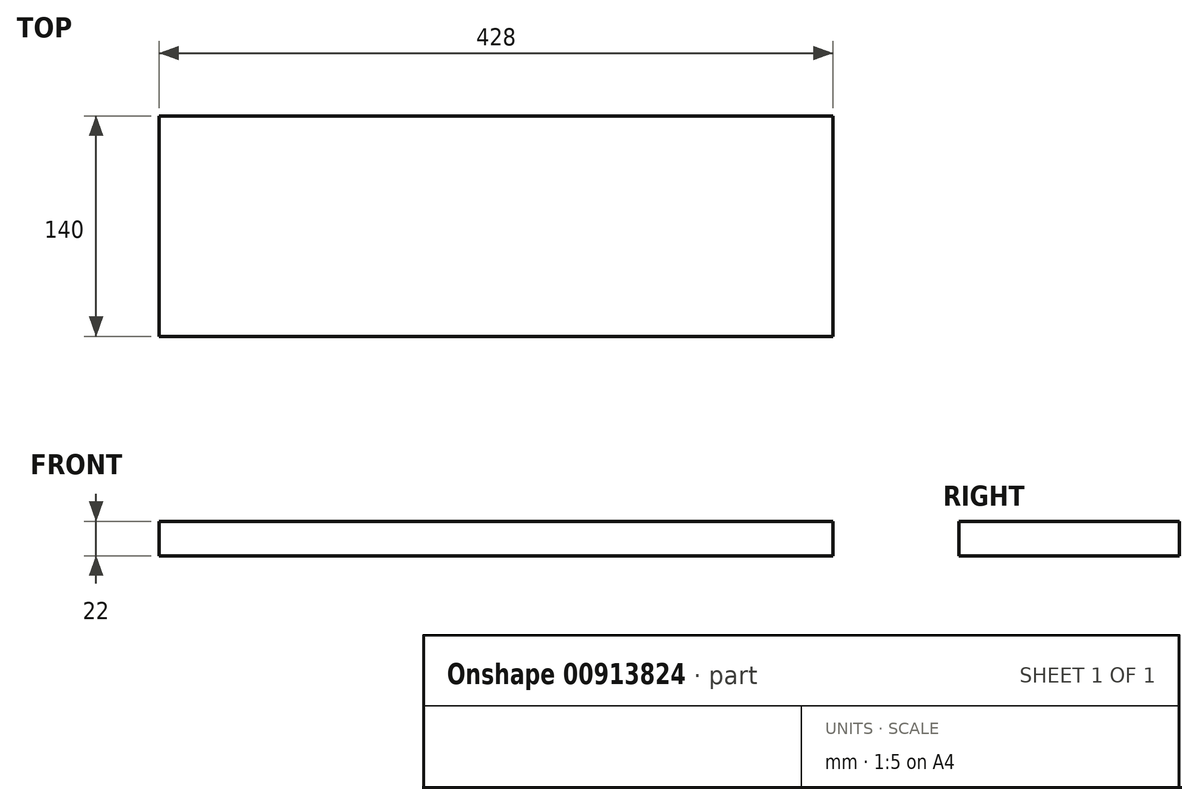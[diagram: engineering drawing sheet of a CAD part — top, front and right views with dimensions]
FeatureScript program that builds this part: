
annotation { "Feature Type Name" : "Feature", "Feature Type Description" : "" }
export const myFeature = defineFeature(function(context is Context, id is Id, definition is map)
    precondition{}
    {
        {
            var Q0;
            Q0=qCreatedBy(makeId("Top.planeOp"),FACE);
            var sketch = newSketch(context, id + "F0", { "sketchPlane" : qUnion([Q0])});
            skLineSegment(sketch, "E0.bottom", {"start": v(214, -70) * mm, "end": v(-214, -70) * mm});
            skLineSegment(sketch, "E0.top", {"start": v(214, 70) * mm, "end": v(-214, 70) * mm});
            skLineSegment(sketch, "E0.left", {"start": v(214, -70) * mm, "end": v(214, 70) * mm});
            skLineSegment(sketch, "E0.right", {"start": v(-214, -70) * mm, "end": v(-214, 70) * mm});
            skPoint(sketch, "E0.middle", {"position": v(0, 0) * mm});
            skSolve(sketch);
        }
        {
            var Q0;
            Q0=makeQuery(id+"F0.imprint","IMPRINT",FACE,{"disambiguationData":[TD([[makeQuery(id+"F0.imprint","IMPRINT",EDGE,{"derivedFrom":sQuery(id+"F0.wireOp",EDGE,"E0.bottom")}),-1.0]])]});
            extrude(context, id + "F1", {"entities" : qUnion([Q0]), "depth" : 22 * mm, "offsetDistance" : 25 * mm});
        }
    });
